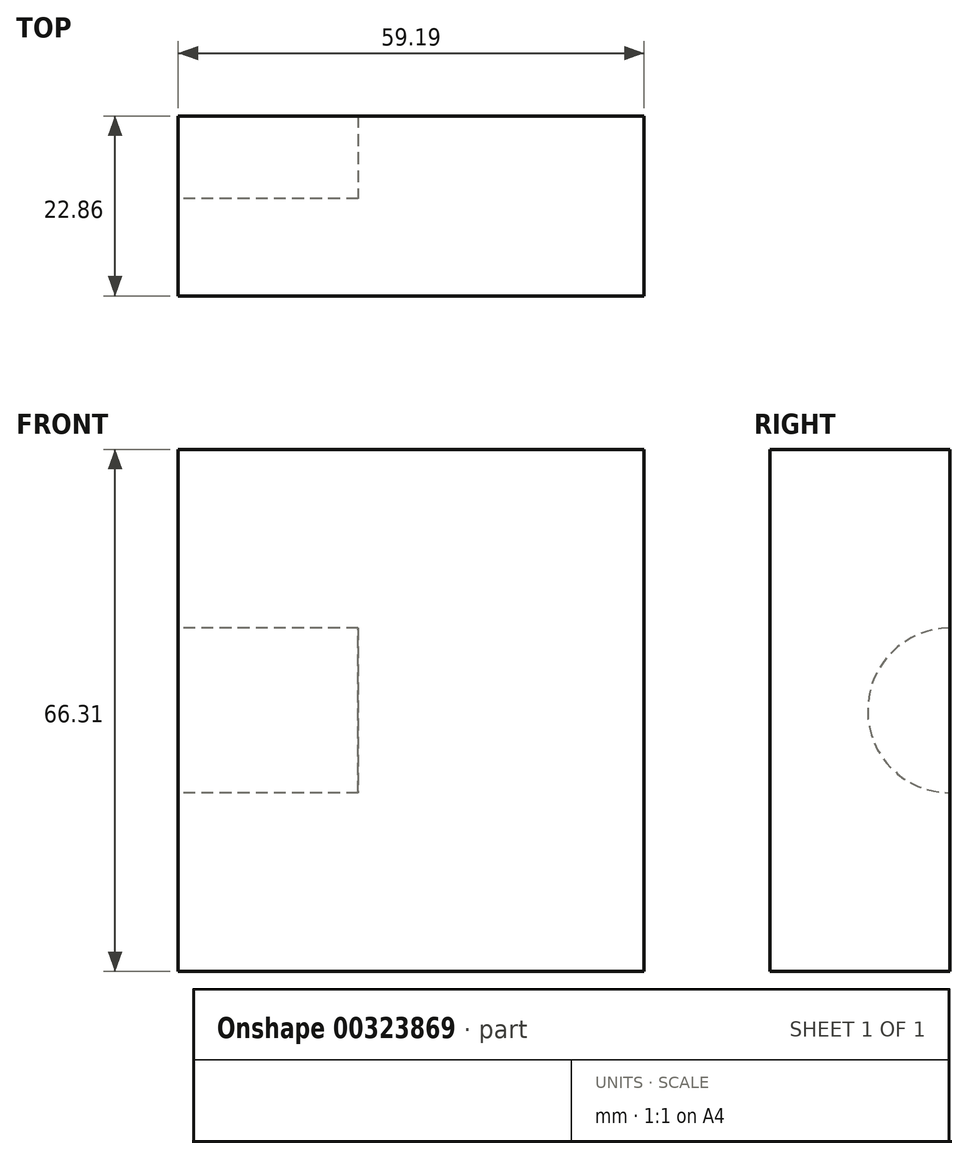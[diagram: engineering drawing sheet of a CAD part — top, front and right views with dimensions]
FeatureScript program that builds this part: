
annotation { "Feature Type Name" : "Feature", "Feature Type Description" : "" }
export const myFeature = defineFeature(function(context is Context, id is Id, definition is map)
    precondition{}
    {
        {
            var Q0;
            Q0=qCreatedBy(makeId("Front.planeOp"),FACE);
            var sketch = newSketch(context, id + "F0", { "sketchPlane" : qUnion([Q0])});
            skLineSegment(sketch, "E0.bottom", {"start": v(-133.97, 16.74) * mm, "end": v(-74.78, 16.74) * mm});
            skLineSegment(sketch, "E0.top", {"start": v(-133.97, -49.57) * mm, "end": v(-74.78, -49.57) * mm});
            skLineSegment(sketch, "E0.left", {"start": v(-133.97, 16.74) * mm, "end": v(-133.97, -49.57) * mm});
            skLineSegment(sketch, "E0.right", {"start": v(-74.78, 16.74) * mm, "end": v(-74.78, -49.57) * mm});
            skSolve(sketch);
        }
        {
            var Q0;
            Q0 = qSketchRegion(id + "F0", true);
            extrude(context, id + "F1", {"entities" : qUnion([Q0]), "depth" : 22.86 * mm});
        }
        {
            var Q0;
            Q0=makeQuery(id+"F1.opExtrude","SWEPT_FACE",FACE,{"disambiguationData":[OSD([sQuery(id+"F0.wireOp",EDGE,"E0.left")])]});
            var sketch = newSketch(context, id + "F2", { "sketchPlane" : qUnion([Q0])});
            skCircle(sketch, "E1", {"center": v(0, -16.41) * mm, "radius": 10.46 * mm});
            skSolve(sketch);
        }
        {
            var Q0;
            Q0 = qSketchRegion(id + "F2", true);
            extrude(context, id + "F3", {"entities" : qUnion([Q0]), "operationType" : NewBodyOperationType.REMOVE, "oppositeDirection" : true, "depth" : 22.86 * mm});
        }
    });
